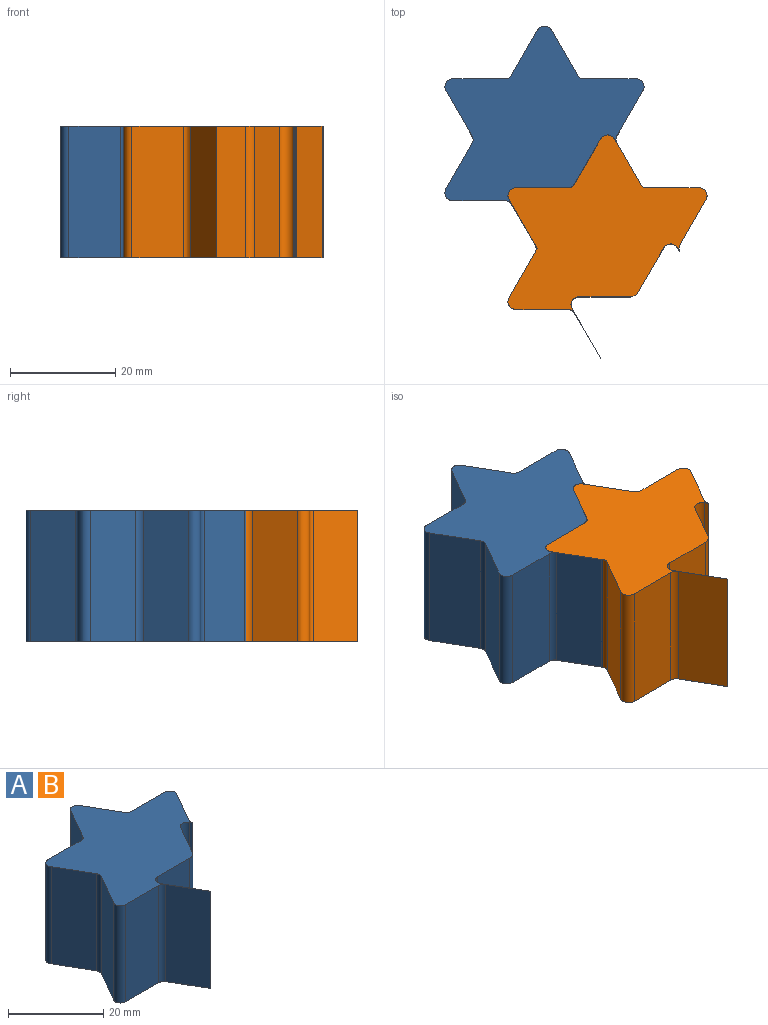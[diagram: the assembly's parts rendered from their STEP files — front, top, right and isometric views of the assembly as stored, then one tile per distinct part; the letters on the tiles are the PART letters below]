
ASSEMBLY  parts=2 mates=1
PART A: 28 faces, bbox 37.8x42.3x25 mm
  f0: plane 25x8.41mm, normal (-0.87,-0.5,0), area 242.8mm2, adj f10,f11,f15,f20
  f1: cylinder r=1.5mm len=25mm, axis (0,0,1), area 33.3mm2, adj f2,f10,f11,f21
  f2: plane 25x8.55mm, normal (0.87,-0.5,0), area 246.7mm2, adj f1,f10,f11,f17
  f3: plane 25x9.87mm, normal (0,1,0), area 246.7mm2, adj f10,f11,f12,f17
  f4: plane 25x8.55mm, normal (0.87,0.5,0), area 246.7mm2, adj f10,f11,f12,f16
  f5: plane 25x8.55mm, normal (-0.87,0.5,0), area 246.7mm2, adj f10,f11,f13,f16
  f6: plane 25x9.87mm, normal (0,1,0), area 246.7mm2, adj f10,f11,f13,f19
  f7: plane 25x8.55mm, normal (-0.87,-0.5,0), area 246.7mm2, adj f10,f11,f14,f19
  f8: plane 25x8.55mm, normal (-0.87,0.5,0), area 246.7mm2, adj f10,f11,f14,f18
  f9: plane 25x9.87mm, normal (0,-1,0), area 246.7mm2, adj f10,f11,f15,f18
  f10: plane 42.3x37.8mm, normal (0,0,1), area 703.4mm2, adj f0,f1,f2,f3,f4,f5,f6,f7
  f11: plane 42.3x37.8mm, normal (0,0,-1), area 703.4mm2, adj f0,f1,f2,f3,f4,f5,f6,f7
  f12: cylinder r=1.5mm len=25mm, axis (0,0,1), area 39.3mm2, adj f3,f4,f10,f11
  f13: cylinder r=1.5mm len=25mm, axis (0,0,1), area 39.3mm2, adj f5,f6,f10,f11
  f14: cylinder r=1.5mm len=25mm, axis (0,0,1), area 39.3mm2, adj f7,f8,f10,f11
  f15: cylinder r=1.5mm len=25mm, axis (0,0,1), area 39.3mm2, adj f0,f9,f10,f11
  f16: cylinder r=1.5mm len=25mm, axis (0,0,-1), area 78.5mm2, adj f4,f5,f10,f11
  f17: cylinder r=1.5mm len=25mm, axis (0,0,-1), area 78.5mm2, adj f2,f3,f10,f11
  f18: cylinder r=1.5mm len=25mm, axis (0,0,-1), area 78.5mm2, adj f8,f9,f10,f11
  f19: cylinder r=1.5mm len=25mm, axis (0,0,-1), area 78.5mm2, adj f6,f7,f10,f11
  f20: plane 25x0.02mm, normal (0.87,-0.5,0), area 0.6mm2, adj f0,f10,f11,f26
  f21: plane 25x0.69mm, normal (-0.87,-0.5,0), area 19.9mm2, adj f1,f10,f11,f22
  f22: cylinder r=1.5mm len=25mm, axis (0,0,-1), area 78.5mm2, adj f10,f11,f21,f23
  f23: plane 25x8.3mm, normal (0.87,-0.5,0), area 239.5mm2, adj f10,f11,f22,f27
  f24: plane 25x9.58mm, normal (0,-1,0), area 239.5mm2, adj f10,f11,f25,f27
  f25: cylinder r=1.5mm len=25mm, axis (0,0,-1), area 78.5mm2, adj f10,f11,f24,f26
  f26: plane 25x9.3mm, normal (0.87,0.5,0), area 268.4mm2, adj f10,f11,f20,f25
  f27: cylinder r=2mm len=25mm, axis (0,0,-1), area 52.4mm2, adj f10,f11,f23,f24
PART B: same geometry as A
PLACE A t=(11.15,-10.04,15.46)mm
PLACE B t=(23.11,-30.73,15.46)mm
MATE cylindrical B.f19 <-> A.f25  axis (0,0,-1) through (-33.71,-9.13,27.96)mm
